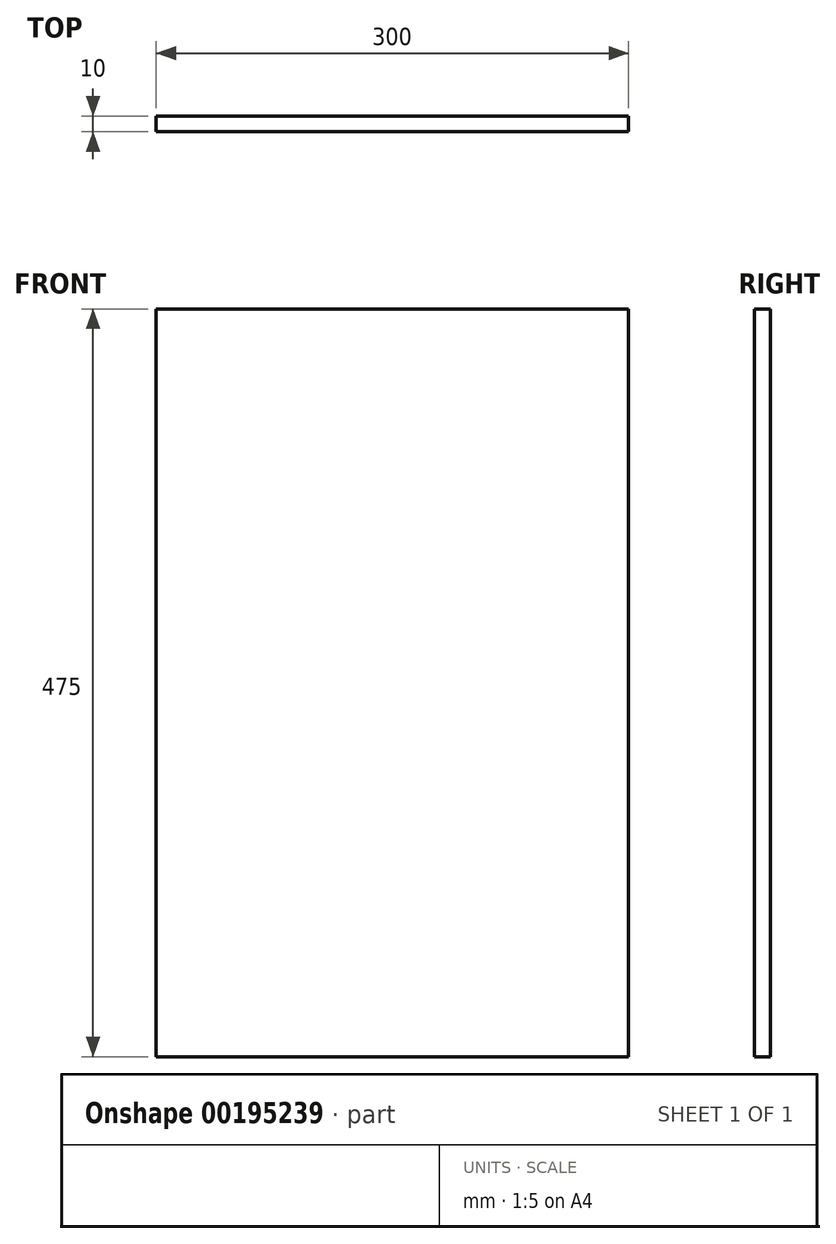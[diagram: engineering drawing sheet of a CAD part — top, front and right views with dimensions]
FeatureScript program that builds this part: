
annotation { "Feature Type Name" : "Feature", "Feature Type Description" : "" }
export const myFeature = defineFeature(function(context is Context, id is Id, definition is map)
    precondition{}
    {
        {
            var Q0;
            Q0=qCreatedBy(makeId("Front.planeOp"),FACE);
            var sketch = newSketch(context, id + "F0", { "sketchPlane" : qUnion([Q0])});
            skLineSegment(sketch, "E0.bottom", {"start": v(-150, 237.5) * mm, "end": v(150, 237.5) * mm});
            skLineSegment(sketch, "E0.top", {"start": v(-150, -237.5) * mm, "end": v(150, -237.5) * mm});
            skLineSegment(sketch, "E0.left", {"start": v(-150, 237.5) * mm, "end": v(-150, -237.5) * mm});
            skLineSegment(sketch, "E0.right", {"start": v(150, 237.5) * mm, "end": v(150, -237.5) * mm});
            skPoint(sketch, "E0.middle", {"position": v(0, 0) * mm});
            skSolve(sketch);
        }
        {
            var Q0;
            Q0=makeQuery(id+"F0.imprint","IMPRINT",FACE,{"disambiguationData":[TD([[makeQuery(id+"F0.imprint","IMPRINT",EDGE,{"derivedFrom":sQuery(id+"F0.wireOp",EDGE,"E0.bottom")}),-1.0]])]});
            extrude(context, id + "F1", {"entities" : qUnion([Q0]), "depth" : 10 * mm});
        }
    });
